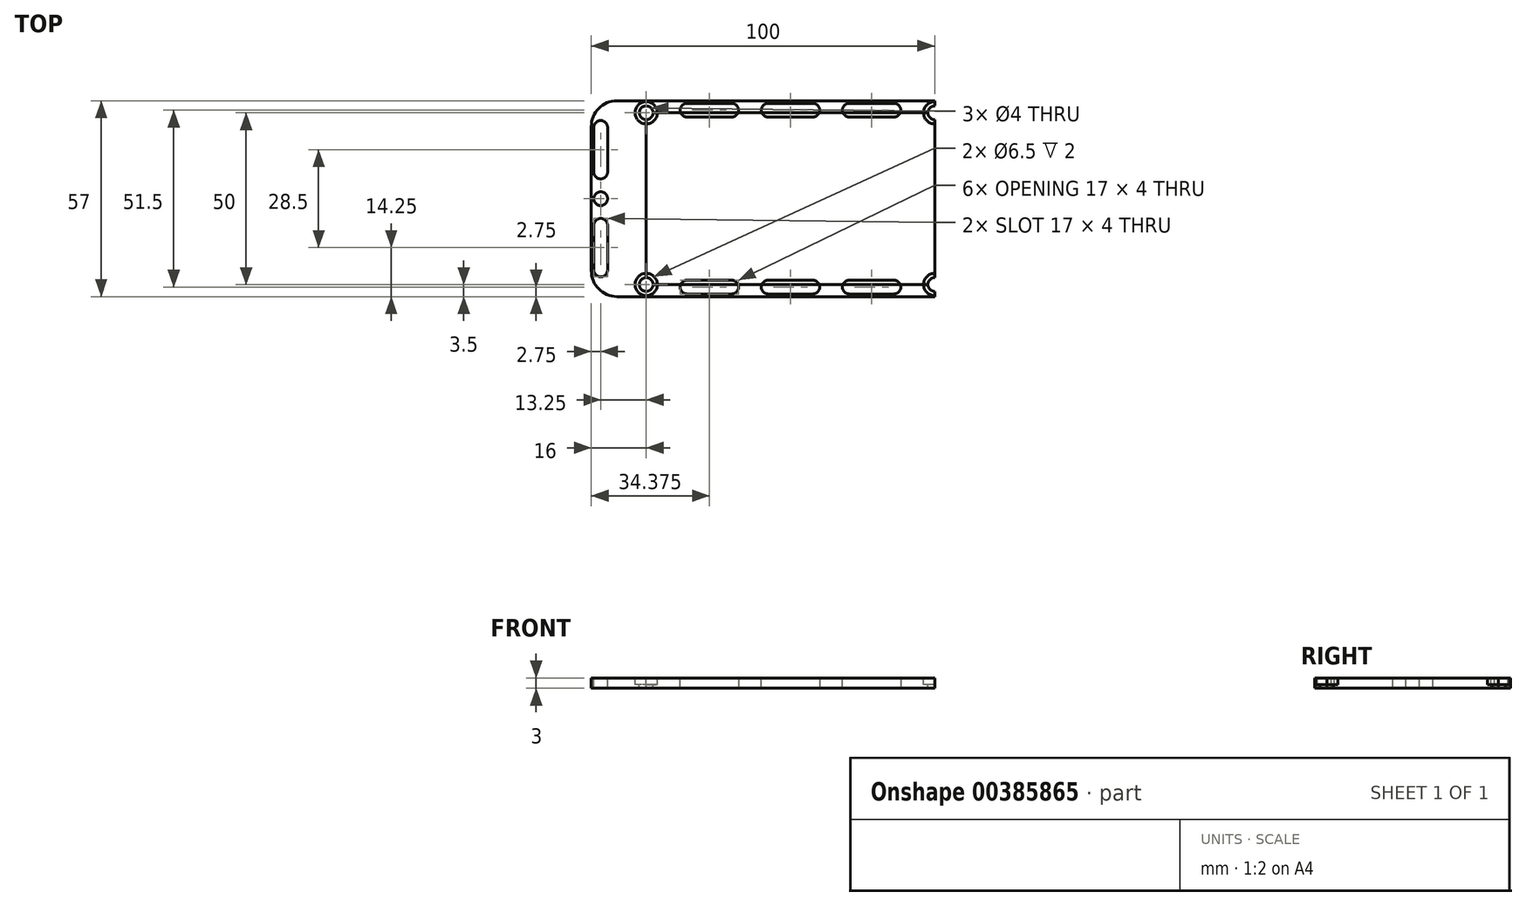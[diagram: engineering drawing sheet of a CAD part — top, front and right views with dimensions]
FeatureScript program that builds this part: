
annotation { "Feature Type Name" : "Feature", "Feature Type Description" : "" }
export const myFeature = defineFeature(function(context is Context, id is Id, definition is map)
    precondition{}
    {
        {
            var Q0;
            Q0=qCreatedBy(makeId("Top.planeOp"),FACE);
            var sketch = newSketch(context, id + "F0", { "sketchPlane" : qUnion([Q0])});
            skLineSegment(sketch, "E0.bottom", {"start": v(0, -28.5) * mm, "end": v(-100, -28.5) * mm});
            skLineSegment(sketch, "E0.top", {"start": v(0, 28.5) * mm, "end": v(-100, 28.5) * mm});
            skLineSegment(sketch, "E0.left", {"start": v(0, -28.5) * mm, "end": v(0, 28.5) * mm});
            skLineSegment(sketch, "E0.right", {"start": v(-100, -28.5) * mm, "end": v(-100, 28.5) * mm});
            skPoint(sketch, "E0.middle", {"position": v(0, 0) * mm});
            skPoint(sketch, "E1", {"position": v(-97.75, 0) * mm});
            skLineSegment(sketch, "E2", {"start": v(-97.75, 0) * mm, "end": v(-97.75, -28.5) * mm});
            skLineSegment(sketch, "E3", {"start": v(-97.75, -28.5) * mm, "end": v(-97.75, 0) * mm});
            skLineSegment(sketch, "E4", {"start": v(-97.75, 0) * mm, "end": v(-97.75, 28.5) * mm});
            skLineSegment(sketch, "E5.bottom", {"start": v(-95.25, 5.75) * mm, "end": v(-99.25, 5.75) * mm});
            skLineSegment(sketch, "E5.top", {"start": v(-95.25, 22.75) * mm, "end": v(-99.25, 22.75) * mm});
            skLineSegment(sketch, "E5.left", {"start": v(-95.25, 5.75) * mm, "end": v(-95.25, 22.75) * mm});
            skLineSegment(sketch, "E5.right", {"start": v(-99.25, 5.75) * mm, "end": v(-99.25, 22.75) * mm});
            skPoint(sketch, "E5.middle", {"position": v(-97.75, 14.25) * mm});
            skLineSegment(sketch, "E6.bottom", {"start": v(-95.25, -22.75) * mm, "end": v(-99.25, -22.75) * mm});
            skLineSegment(sketch, "E6.top", {"start": v(-95.25, -5.75) * mm, "end": v(-99.25, -5.75) * mm});
            skLineSegment(sketch, "E6.left", {"start": v(-95.25, -22.75) * mm, "end": v(-95.25, -5.75) * mm});
            skLineSegment(sketch, "E6.right", {"start": v(-99.25, -22.75) * mm, "end": v(-99.25, -5.75) * mm});
            skPoint(sketch, "E6.middle", {"position": v(-97.75, -14.25) * mm});
            skPoint(sketch, "E7", {"position": v(-97.25, 0) * mm});
            skLineSegment(sketch, "E8", {"start": v(-97.75, 25.8) * mm, "end": v(-80.75, 25.8) * mm});
            skLineSegment(sketch, "E9", {"start": v(-3.25, 25.8) * mm, "end": v(0, 25.8) * mm});
            skLineSegment(sketch, "E10.bottom", {"start": v(-50.5, 27.75) * mm, "end": v(-33.5, 27.75) * mm});
            skLineSegment(sketch, "E10.top", {"start": v(-50.5, 23.75) * mm, "end": v(-33.5, 23.75) * mm});
            skLineSegment(sketch, "E10.left", {"start": v(-50.5, 27.75) * mm, "end": v(-50.5, 23.75) * mm});
            skLineSegment(sketch, "E10.right", {"start": v(-33.5, 27.75) * mm, "end": v(-33.5, 23.75) * mm});
            skLineSegment(sketch, "E11.bottom", {"start": v(-26.88, 27.75) * mm, "end": v(-9.88, 27.75) * mm});
            skLineSegment(sketch, "E11.top", {"start": v(-26.88, 23.75) * mm, "end": v(-9.88, 23.75) * mm});
            skLineSegment(sketch, "E11.left", {"start": v(-26.88, 27.75) * mm, "end": v(-26.88, 23.75) * mm});
            skLineSegment(sketch, "E11.right", {"start": v(-9.88, 27.75) * mm, "end": v(-9.88, 23.75) * mm});
            skLineSegment(sketch, "E12.bottom", {"start": v(-74.13, 27.75) * mm, "end": v(-57.13, 27.75) * mm});
            skLineSegment(sketch, "E12.top", {"start": v(-74.13, 23.75) * mm, "end": v(-57.13, 23.75) * mm});
            skLineSegment(sketch, "E12.left", {"start": v(-74.13, 27.75) * mm, "end": v(-74.13, 23.75) * mm});
            skLineSegment(sketch, "E12.right", {"start": v(-57.13, 27.75) * mm, "end": v(-57.13, 23.75) * mm});
            skLineSegment(sketch, "E13.bottom", {"start": v(-50.5, -23.75) * mm, "end": v(-33.5, -23.75) * mm});
            skLineSegment(sketch, "E13.top", {"start": v(-50.5, -27.75) * mm, "end": v(-33.5, -27.75) * mm});
            skLineSegment(sketch, "E13.left", {"start": v(-50.5, -23.75) * mm, "end": v(-50.5, -27.75) * mm});
            skLineSegment(sketch, "E13.right", {"start": v(-33.5, -23.75) * mm, "end": v(-33.5, -27.75) * mm});
            skLineSegment(sketch, "E14.bottom", {"start": v(-26.88, -23.75) * mm, "end": v(-9.88, -23.75) * mm});
            skLineSegment(sketch, "E14.top", {"start": v(-26.88, -27.75) * mm, "end": v(-9.88, -27.75) * mm});
            skLineSegment(sketch, "E14.left", {"start": v(-26.88, -23.75) * mm, "end": v(-26.88, -27.75) * mm});
            skLineSegment(sketch, "E14.right", {"start": v(-9.88, -23.75) * mm, "end": v(-9.88, -27.75) * mm});
            skLineSegment(sketch, "E15.bottom", {"start": v(-74.12, -23.75) * mm, "end": v(-57.12, -23.75) * mm});
            skLineSegment(sketch, "E15.top", {"start": v(-74.12, -27.75) * mm, "end": v(-57.12, -27.75) * mm});
            skLineSegment(sketch, "E15.left", {"start": v(-74.13, -23.75) * mm, "end": v(-74.13, -27.75) * mm});
            skLineSegment(sketch, "E15.right", {"start": v(-57.13, -23.75) * mm, "end": v(-57.13, -27.75) * mm});
            skSolve(sketch);
        }
        {
            var Q0;
            Q0=qCreatedBy(makeId("Top.planeOp"),FACE);
            var sketch = newSketch(context, id + "F1", { "sketchPlane" : qUnion([Q0])});
            skLineSegment(sketch, "E16.bottom", {"start": v(-84, 25) * mm, "end": v(0, 25) * mm});
            skLineSegment(sketch, "E16.top", {"start": v(-84, -25) * mm, "end": v(0, -25) * mm});
            skLineSegment(sketch, "E16.left", {"start": v(-84, 25) * mm, "end": v(-84, -25) * mm});
            skLineSegment(sketch, "E16.right", {"start": v(0, 25) * mm, "end": v(0, -25) * mm});
            skPoint(sketch, "E16.middle", {"position": v(0, 0) * mm});
            skSolve(sketch);
        }
        {
            var Q0;
            Q0=qSketchRegion(id+"F1",true);
            var Q1;
            Q1=qSketchRegion(id+"F0",true);
            var Q2;
            Q2=sQuery(id+"F1.wireOp",EDGE,"E16.top");
            var Q3;
            Q3=sQuery(id+"F0.wireOp",EDGE,"E0.bottom");
            var Q4;
            Q4=sQuery(id+"F0.wireOp",EDGE,"E0.right");
            var Q5;
            Q5=sQuery(id+"F1.wireOp",EDGE,"E16.left");
            var Q6;
            Q6=sQuery(id+"F1.wireOp",EDGE,"E16.bottom");
            var Q7;
            Q7=sQuery(id+"F0.wireOp",EDGE,"E0.top");
            var Q8;
            Q8=sQuery(id+"F1.wireOp",EDGE,"E16.right");
            var Q9;
            Q9=sQuery(id+"F0.wireOp",EDGE,"E0.left");
            extrude(context, id + "F2", {"entities" : qUnion([Q0, Q1]), "surfaceEntities" : qUnion([Q2, Q3, Q4, Q5, Q6, Q7, Q8, Q9]), "oppositeDirection" : true, "depth" : 3 * mm});
        }
        {
            var Q0;
            Q0=sQuery(id+"F1.wireOp",VERTEX,"E16.left.start");
            var Q1;
            Q1=sQuery(id+"F1.wireOp",VERTEX,"E16.right.start");
            var Q2;
            Q2=sQuery(id+"F1.wireOp",VERTEX,"E16.right.end");
            var Q3;
            Q3=sQuery(id+"F1.wireOp",VERTEX,"E16.left.end");
            var Q4;
            Q4=makeQuery(id+"F2.opExtrude","SWEPT_BODY",BODY,{"disambiguationData":[OSD([sQuery(id+"F0.wireOp",EDGE,"E0.bottom"),sQuery(id+"F0.wireOp",EDGE,"E0.top"),sQuery(id+"F0.wireOp",EDGE,"E0.left"),sQuery(id+"F0.wireOp",EDGE,"E0.right")])]});
            var Q5;
            Q5=makeQuery(id+"F2.opExtrude","SWEPT_BODY",BODY,{"disambiguationData":[OSD([sQuery(id+"F1.wireOp",EDGE,"E16.bottom"),sQuery(id+"F1.wireOp",EDGE,"E16.top"),sQuery(id+"F1.wireOp",EDGE,"E16.left"),sQuery(id+"F1.wireOp",EDGE,"E16.right")])]});
            hole(context, id + "F3", {"style" : HoleStyle.C_BORE, "endStyle" : HoleEndStyle.BLIND, "holeDiameter" : 4 * mm, "cBoreDiameter" : 6.5 * mm, "cBoreDepth" : 2 * mm, "holeDepth" : 3 * mm, "isTappedThrough" : true, "tappedDepth" : 12 * mm, "tapClearance" : 3, "startFromSketch" : true, "locations" : qUnion([Q0, Q1, Q2, Q3]), "scope" : qUnion([Q4, Q5])});
        }
        {
            var Q0;
            Q0=sQuery(id+"F0.wireOp",VERTEX,"E7");
            var Q1;
            Q1=makeQuery(id+"F2.opExtrude","SWEPT_BODY",BODY,{"disambiguationData":[OSD([sQuery(id+"F0.wireOp",EDGE,"E0.bottom"),sQuery(id+"F0.wireOp",EDGE,"E0.top"),sQuery(id+"F0.wireOp",EDGE,"E0.left"),sQuery(id+"F0.wireOp",EDGE,"E0.right")])]});
            hole(context, id + "F4", {"style" : HoleStyle.SIMPLE, "endStyle" : HoleEndStyle.THROUGH, "holeDiameter" : 4 * mm, "isTappedThrough" : true, "tappedDepth" : 12 * mm, "tapClearance" : 3, "startFromSketch" : true, "locations" : qUnion([Q0]), "scope" : qUnion([Q1])});
        }
        {
            var Q0;
            Q0=makeQuery(id+"F2.opExtrude","SWEPT_EDGE",EDGE,{"disambiguationData":[OSD([sQuery(id+"F0.wireOp",EDGE,"E5.top"),sQuery(id+"F0.wireOp",EDGE,"E5.right")])]});
            var Q1;
            Q1=makeQuery(id+"F2.opExtrude","SWEPT_EDGE",EDGE,{"disambiguationData":[OSD([sQuery(id+"F0.wireOp",EDGE,"E5.top"),sQuery(id+"F0.wireOp",EDGE,"E5.left")])]});
            var Q2;
            Q2=makeQuery(id+"F2.opExtrude","SWEPT_EDGE",EDGE,{"disambiguationData":[OSD([sQuery(id+"F0.wireOp",EDGE,"E5.bottom"),sQuery(id+"F0.wireOp",EDGE,"E5.right")])]});
            var Q3;
            Q3=makeQuery(id+"F2.opExtrude","SWEPT_EDGE",EDGE,{"disambiguationData":[OSD([sQuery(id+"F0.wireOp",EDGE,"E5.bottom"),sQuery(id+"F0.wireOp",EDGE,"E5.left")])]});
            var Q4;
            Q4=makeQuery(id+"F2.opExtrude","SWEPT_EDGE",EDGE,{"disambiguationData":[OSD([sQuery(id+"F0.wireOp",EDGE,"E6.top"),sQuery(id+"F0.wireOp",EDGE,"E6.right")])]});
            var Q5;
            Q5=makeQuery(id+"F2.opExtrude","SWEPT_EDGE",EDGE,{"disambiguationData":[OSD([sQuery(id+"F0.wireOp",EDGE,"E6.top"),sQuery(id+"F0.wireOp",EDGE,"E6.left")])]});
            var Q6;
            Q6=makeQuery(id+"F2.opExtrude","SWEPT_EDGE",EDGE,{"disambiguationData":[OSD([sQuery(id+"F0.wireOp",EDGE,"E6.bottom"),sQuery(id+"F0.wireOp",EDGE,"E6.left")])]});
            var Q7;
            Q7=makeQuery(id+"F2.opExtrude","SWEPT_EDGE",EDGE,{"disambiguationData":[OSD([sQuery(id+"F0.wireOp",EDGE,"E6.bottom"),sQuery(id+"F0.wireOp",EDGE,"E6.right")])]});
            var Q8;
            Q8=makeQuery(id+"F2.opExtrude","SWEPT_EDGE",EDGE,{"disambiguationData":[OSD([sQuery(id+"F0.wireOp",EDGE,"E15.top"),sQuery(id+"F0.wireOp",EDGE,"E15.left")])]});
            var Q9;
            Q9=makeQuery(id+"F2.opExtrude","SWEPT_EDGE",EDGE,{"disambiguationData":[OSD([sQuery(id+"F0.wireOp",EDGE,"E13.top"),sQuery(id+"F0.wireOp",EDGE,"E13.left")])]});
            var Q10;
            Q10=makeQuery(id+"F2.opExtrude","SWEPT_EDGE",EDGE,{"disambiguationData":[OSD([sQuery(id+"F0.wireOp",EDGE,"E15.top"),sQuery(id+"F0.wireOp",EDGE,"E15.right")])]});
            var Q11;
            Q11=makeQuery(id+"F2.opExtrude","SWEPT_EDGE",EDGE,{"disambiguationData":[OSD([sQuery(id+"F0.wireOp",EDGE,"E14.top"),sQuery(id+"F0.wireOp",EDGE,"E14.right")])]});
            var Q12;
            Q12=makeQuery(id+"F2.opExtrude","SWEPT_EDGE",EDGE,{"disambiguationData":[OSD([sQuery(id+"F0.wireOp",EDGE,"E13.top"),sQuery(id+"F0.wireOp",EDGE,"E13.right")])]});
            var Q13;
            Q13=makeQuery(id+"F2.opExtrude","SWEPT_EDGE",EDGE,{"disambiguationData":[OSD([sQuery(id+"F0.wireOp",EDGE,"E14.top"),sQuery(id+"F0.wireOp",EDGE,"E14.left")])]});
            var Q14;
            Q14=makeQuery(id+"F2.opExtrude","SWEPT_EDGE",EDGE,{"disambiguationData":[OSD([sQuery(id+"F0.wireOp",EDGE,"E11.bottom"),sQuery(id+"F0.wireOp",EDGE,"E11.right")])]});
            var Q15;
            Q15=makeQuery(id+"F2.opExtrude","SWEPT_EDGE",EDGE,{"disambiguationData":[OSD([sQuery(id+"F0.wireOp",EDGE,"E10.bottom"),sQuery(id+"F0.wireOp",EDGE,"E10.right")])]});
            var Q16;
            Q16=makeQuery(id+"F2.opExtrude","SWEPT_EDGE",EDGE,{"disambiguationData":[OSD([sQuery(id+"F0.wireOp",EDGE,"E12.bottom"),sQuery(id+"F0.wireOp",EDGE,"E12.right")])]});
            var Q17;
            Q17=makeQuery(id+"F2.opExtrude","SWEPT_EDGE",EDGE,{"disambiguationData":[OSD([sQuery(id+"F0.wireOp",EDGE,"E12.bottom"),sQuery(id+"F0.wireOp",EDGE,"E12.left")])]});
            var Q18;
            Q18=makeQuery(id+"F2.opExtrude","SWEPT_EDGE",EDGE,{"disambiguationData":[OSD([sQuery(id+"F0.wireOp",EDGE,"E10.bottom"),sQuery(id+"F0.wireOp",EDGE,"E10.left")])]});
            var Q19;
            Q19=makeQuery(id+"F2.opExtrude","SWEPT_EDGE",EDGE,{"disambiguationData":[OSD([sQuery(id+"F0.wireOp",EDGE,"E11.bottom"),sQuery(id+"F0.wireOp",EDGE,"E11.left")])]});
            fillet(context, id + "F5", {"entities" : qUnion([Q0, Q1, Q2, Q3, Q4, Q5, Q6, Q7, Q8, Q9, Q10, Q11, Q12, Q13, Q14, Q15, Q16, Q17, Q18, Q19]), "radius" : 2 * mm, "tangentPropagation" : true, "allowEdgeOverflow" : false});
        }
        {
            var Q0;
            Q0=makeQuery(id+"F2.opExtrude","SWEPT_EDGE",EDGE,{"disambiguationData":[OSD([sQuery(id+"F0.wireOp",EDGE,"E12.top"),sQuery(id+"F0.wireOp",EDGE,"E12.left")])]});
            var Q1;
            Q1=makeQuery(id+"F2.opExtrude","SWEPT_EDGE",EDGE,{"disambiguationData":[OSD([sQuery(id+"F0.wireOp",EDGE,"E12.top"),sQuery(id+"F0.wireOp",EDGE,"E12.right")])]});
            var Q2;
            Q2=makeQuery(id+"F2.opExtrude","SWEPT_EDGE",EDGE,{"disambiguationData":[OSD([sQuery(id+"F0.wireOp",EDGE,"E10.top"),sQuery(id+"F0.wireOp",EDGE,"E10.left")])]});
            var Q3;
            Q3=makeQuery(id+"F2.opExtrude","SWEPT_EDGE",EDGE,{"disambiguationData":[OSD([sQuery(id+"F0.wireOp",EDGE,"E10.top"),sQuery(id+"F0.wireOp",EDGE,"E10.right")])]});
            var Q4;
            Q4=makeQuery(id+"F2.opExtrude","SWEPT_EDGE",EDGE,{"disambiguationData":[OSD([sQuery(id+"F0.wireOp",EDGE,"E11.top"),sQuery(id+"F0.wireOp",EDGE,"E11.left")])]});
            var Q5;
            Q5=makeQuery(id+"F2.opExtrude","SWEPT_EDGE",EDGE,{"disambiguationData":[OSD([sQuery(id+"F0.wireOp",EDGE,"E11.top"),sQuery(id+"F0.wireOp",EDGE,"E11.right")])]});
            var Q6;
            Q6=makeQuery(id+"F2.opExtrude","SWEPT_EDGE",EDGE,{"disambiguationData":[OSD([sQuery(id+"F0.wireOp",EDGE,"E14.bottom"),sQuery(id+"F0.wireOp",EDGE,"E14.right")])]});
            var Q7;
            Q7=makeQuery(id+"F2.opExtrude","SWEPT_EDGE",EDGE,{"disambiguationData":[OSD([sQuery(id+"F0.wireOp",EDGE,"E14.bottom"),sQuery(id+"F0.wireOp",EDGE,"E14.left")])]});
            var Q8;
            Q8=makeQuery(id+"F2.opExtrude","SWEPT_EDGE",EDGE,{"disambiguationData":[OSD([sQuery(id+"F0.wireOp",EDGE,"E13.bottom"),sQuery(id+"F0.wireOp",EDGE,"E13.left")])]});
            var Q9;
            Q9=makeQuery(id+"F2.opExtrude","SWEPT_EDGE",EDGE,{"disambiguationData":[OSD([sQuery(id+"F0.wireOp",EDGE,"E13.bottom"),sQuery(id+"F0.wireOp",EDGE,"E13.right")])]});
            var Q10;
            Q10=makeQuery(id+"F2.opExtrude","SWEPT_EDGE",EDGE,{"disambiguationData":[OSD([sQuery(id+"F0.wireOp",EDGE,"E15.bottom"),sQuery(id+"F0.wireOp",EDGE,"E15.right")])]});
            var Q11;
            Q11=makeQuery(id+"F2.opExtrude","SWEPT_EDGE",EDGE,{"disambiguationData":[OSD([sQuery(id+"F0.wireOp",EDGE,"E15.bottom"),sQuery(id+"F0.wireOp",EDGE,"E15.left")])]});
            fillet(context, id + "F6", {"entities" : qUnion([Q0, Q1, Q2, Q3, Q4, Q5, Q6, Q7, Q8, Q9, Q10, Q11]), "radius" : 2 * mm, "tangentPropagation" : true, "allowEdgeOverflow" : false});
        }
        {
            var Q0;
            Q0=makeQuery(id+"F2.opExtrude","SWEPT_EDGE",EDGE,{"disambiguationData":[OSD([sQuery(id+"F0.wireOp",EDGE,"E0.top"),sQuery(id+"F0.wireOp",EDGE,"E0.right")])]});
            var Q1;
            Q1=makeQuery(id+"F2.opExtrude","SWEPT_EDGE",EDGE,{"disambiguationData":[OSD([sQuery(id+"F0.wireOp",EDGE,"E0.bottom"),sQuery(id+"F0.wireOp",EDGE,"E0.right")])]});
            fillet(context, id + "F7", {"entities" : qUnion([Q0, Q1]), "radius" : 7.5 * mm, "tangentPropagation" : true, "allowEdgeOverflow" : false});
        }
    });
